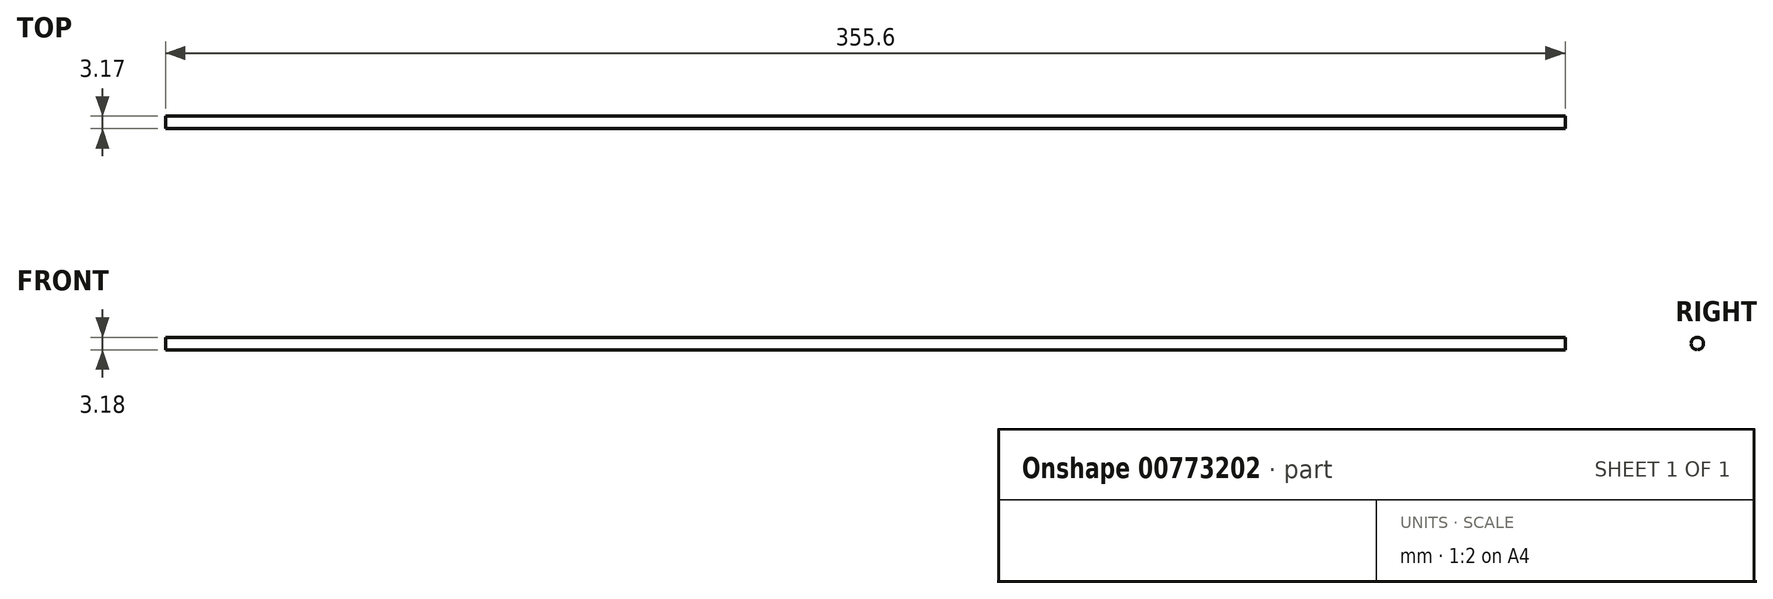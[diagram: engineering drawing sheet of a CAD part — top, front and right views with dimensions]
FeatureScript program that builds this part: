
annotation { "Feature Type Name" : "Feature", "Feature Type Description" : "" }
export const myFeature = defineFeature(function(context is Context, id is Id, definition is map)
    precondition{}
    {
        {
            var Q0;
            Q0=qCreatedBy(makeId("Right.planeOp"),FACE);
            var sketch = newSketch(context, id + "F0", { "sketchPlane" : qUnion([Q0])});
            skCircle(sketch, "E0", {"center": v(-29.44, 27.6) * mm, "radius": 1.59 * mm});
            skSolve(sketch);
        }
        {
            var Q0;
            Q0 = qSketchRegion(id + "F0", true);
            extrude(context, id + "F1", {"entities" : qUnion([Q0]), "depth" : 355.6 * mm, "offsetDistance" : 25.4 * mm});
        }
    });
